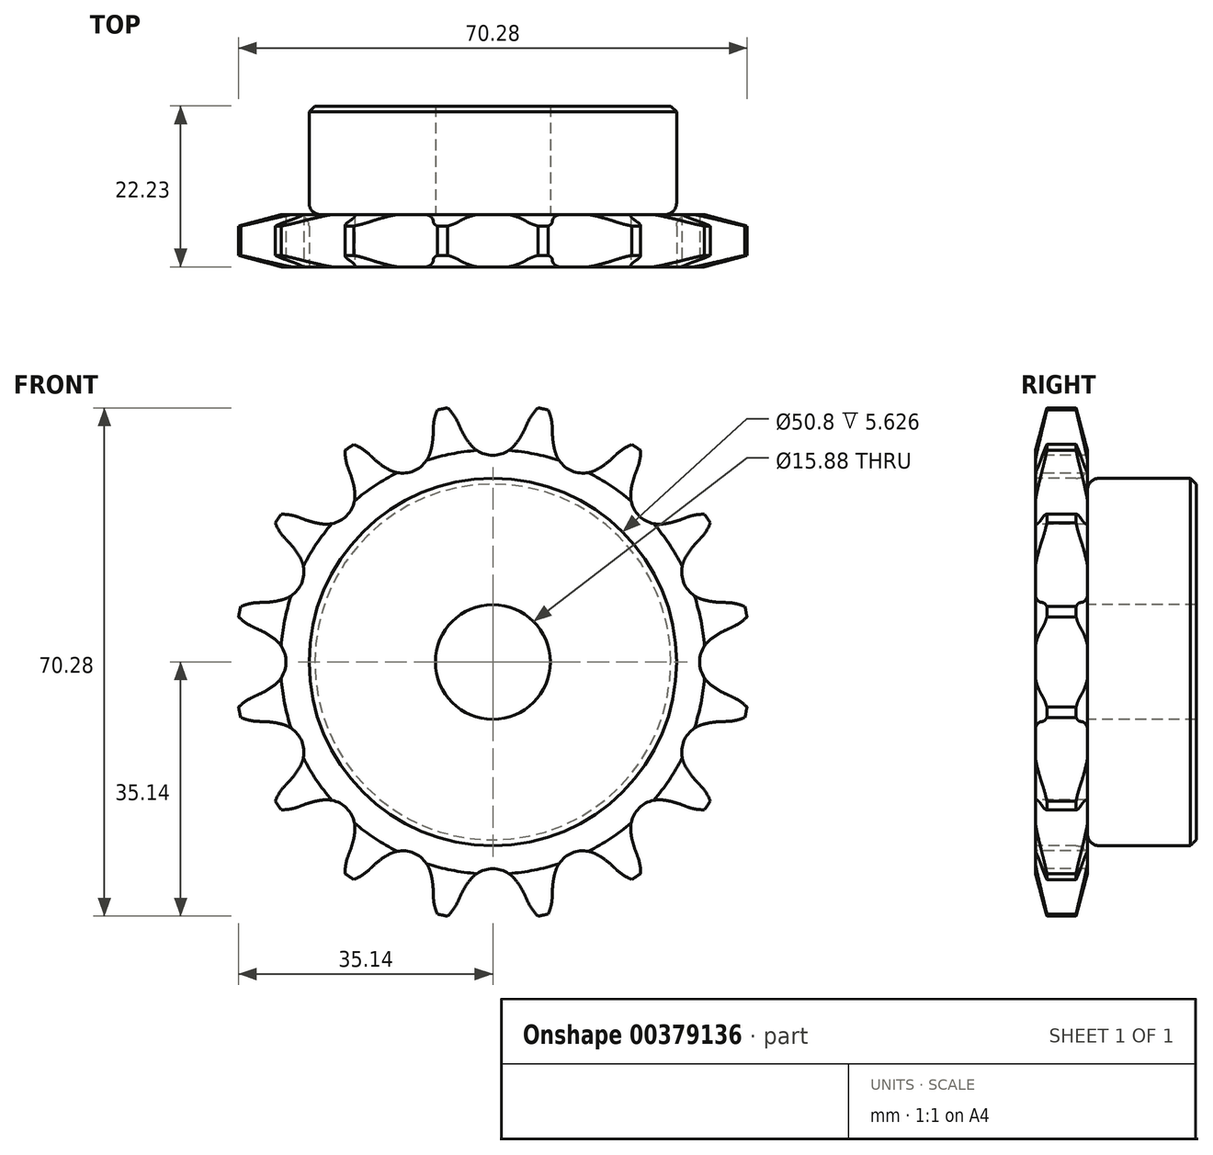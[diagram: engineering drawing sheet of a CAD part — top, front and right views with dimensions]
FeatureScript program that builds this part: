
annotation { "Feature Type Name" : "Feature", "Feature Type Description" : "" }
export const myFeature = defineFeature(function(context is Context, id is Id, definition is map)
    precondition{}
    {
        {
            var Q0;
            Q0=qCreatedBy(makeId("Right.planeOp"),FACE);
            var sketch = newSketch(context, id + "F0", { "sketchPlane" : qUnion([Q0])});
            skLineSegment(sketch, "E0", {"start": v(0, 0) * mm, "end": v(37.55, 0) * mm, "construction": true});
            skLineSegment(sketch, "E1.bottom", {"start": v(0, 7.94) * mm, "end": v(7.21, 7.94) * mm});
            skLineSegment(sketch, "E1.top", {"start": v(0, 35.69) * mm, "end": v(7.21, 35.69) * mm});
            skLineSegment(sketch, "E1.left", {"start": v(0, 7.94) * mm, "end": v(0, 35.69) * mm});
            skLineSegment(sketch, "E1.right", {"start": v(7.21, 7.94) * mm, "end": v(7.21, 35.69) * mm});
            skLineSegment(sketch, "E2.bottom", {"start": v(0, 7.94) * mm, "end": v(22.23, 7.94) * mm});
            skLineSegment(sketch, "E2.top", {"start": v(0, 25.4) * mm, "end": v(22.22, 25.4) * mm});
            skLineSegment(sketch, "E2.left", {"start": v(0, 7.94) * mm, "end": v(0, 25.4) * mm});
            skLineSegment(sketch, "E2.right", {"start": v(22.23, 7.94) * mm, "end": v(22.22, 25.4) * mm});
            skLineSegment(sketch, "E3.MirrorCS", {"start": v(0, -7.94) * mm, "end": v(7.21, -7.94) * mm});
            skLineSegment(sketch, "E4.MirrorCS", {"start": v(22.23, -7.94) * mm, "end": v(22.23, -25.4) * mm});
            skLineSegment(sketch, "E5.MirrorCS", {"start": v(0, -7.94) * mm, "end": v(0, -25.4) * mm});
            skLineSegment(sketch, "E6.MirrorCS", {"start": v(0, -25.4) * mm, "end": v(22.22, -25.4) * mm});
            skLineSegment(sketch, "E7.MirrorCS", {"start": v(0, -7.94) * mm, "end": v(22.23, -7.94) * mm});
            skLineSegment(sketch, "E8.MirrorCS", {"start": v(7.21, -7.94) * mm, "end": v(7.21, -35.69) * mm});
            skLineSegment(sketch, "E9.MirrorCS", {"start": v(0, -7.94) * mm, "end": v(0, -35.69) * mm});
            skLineSegment(sketch, "E10.MirrorCS", {"start": v(0, -35.69) * mm, "end": v(7.21, -35.69) * mm});
            skSolve(sketch);
        }
        {
            var Q0;
            {var subQ5=sQuery(id+"F0.wireOp",EDGE,"E2.right");Q0=makeQuery(id+"F0.imprint","IMPRINT",FACE,{"disambiguationData":[TD([[makeQuery(id+"F0.imprint","IMPRINT",EDGE,{"derivedFrom":subQ5}),1.0]])]});}
            var Q1;
            {var subQ5=sQuery(id+"F0.wireOp",EDGE,"E2.left");Q1=makeQuery(id+"F0.imprint","IMPRINT",FACE,{"disambiguationData":[TD([[makeQuery(id+"F0.imprint","IMPRINT",EDGE,{"derivedFrom":subQ5}),-1.0]])]});}
            var Q2;
            {var subQ0=sQuery(id+"F0.wireOp",EDGE,"E1.top");Q2=makeQuery(id+"F0.imprint","IMPRINT",FACE,{"disambiguationData":[TD([[makeQuery(id+"F0.imprint","IMPRINT",EDGE,{"derivedFrom":subQ0}),-1.0]])]});}
            var Q3;
            Q3=sQuery(id+"F0.wireOp",EDGE,"E0");
            revolve(context, id + "F1", {"entities" : qUnion([Q0, Q1, Q2]), "axis" : qUnion([Q3]), "revolveType" : RevolveType.FULL});
        }
        {
            var Q0;
            Q0=makeQuery(id+"F1.opRevolve","SWEPT_EDGE",EDGE,{"disambiguationData":[OSD([sQuery(id+"F0.wireOp",EDGE,"E1.right"),sQuery(id+"F0.wireOp",EDGE,"E2.top")])]});
            fillet(context, id + "F2", {"entities" : qUnion([Q0]), "radius" : 1.59 * mm, "tangentPropagation" : true, "allowEdgeOverflow" : false});
        }
        {
            var Q0;
            Q0=makeQuery(id+"F1.opRevolve","SWEPT_EDGE",EDGE,{"disambiguationData":[OSD([sQuery(id+"F0.wireOp",EDGE,"E2.top"),sQuery(id+"F0.wireOp",EDGE,"E2.right")])]});
            chamfer(context, id + "F3", {"entities" : qUnion([Q0]), "width" : 0.8 * mm, "tangentPropagation" : true});
        }
        {
            var Q0;
            Q0=makeQuery(id+"F1.opRevolve","SWEPT_EDGE",EDGE,{"disambiguationData":[OSD([sQuery(id+"F0.wireOp",EDGE,"E1.top"),sQuery(id+"F0.wireOp",EDGE,"E1.left")])]});
            var Q1;
            Q1=makeQuery(id+"F1.opRevolve","SWEPT_EDGE",EDGE,{"disambiguationData":[OSD([sQuery(id+"F0.wireOp",EDGE,"E1.top"),sQuery(id+"F0.wireOp",EDGE,"E1.right")])]});
            chamfer(context, id + "F4", {"entities" : qUnion([Q0, Q1]), "chamferType" : ChamferType.TWO_OFFSETS, "width1" : 6.35 * mm, "oppositeDirection" : false, "width2" : 1.59 * mm, "tangentPropagation" : true});
        }
        {
            var Q0;
            Q0=makeQuery(id+"F1.opRevolve","SWEPT_FACE",FACE,{"disambiguationData":[OSD([sQuery(id+"F0.wireOp",EDGE,"E1.left"),sQuery(id+"F0.wireOp",EDGE,"E2.left")])]});
            var sketch = newSketch(context, id + "F5", { "sketchPlane" : qUnion([Q0])});
            skCircle(sketch, "E11", {"center": v(0, 0) * mm, "radius": 32.55 * mm, "construction": true});
            skLineSegment(sketch, "E12", {"start": v(0, 0) * mm, "end": v(0, 32.55) * mm, "construction": true});
            skLineSegment(sketch, "E13", {"start": v(0, 32.55) * mm, "end": v(30.15, 32.55) * mm, "construction": true});
            skLineSegment(sketch, "E14", {"start": v(0, 32.55) * mm, "end": v(5, 36.56) * mm, "construction": true});
            skLineSegment(sketch, "E15", {"start": v(5, 36.56) * mm, "end": v(-4.46, 32.3) * mm, "construction": true});
            skLineSegment(sketch, "E16", {"start": v(-4.46, 32.3) * mm, "end": v(-4.82, 33.1) * mm});
            skLineSegment(sketch, "E17", {"start": v(0, 0) * mm, "end": v(-7.32, 35.97) * mm, "construction": true});
            skArc(sketch, "E18", {"start": v(-7.32, 35.97) * mm, "mid": v(-15.8, 26.06) * mm, "end": v(-4.82, 33.1) * mm, "construction": true});
            skArc(sketch, "E19", {"start": v(-4.82, 33.1) * mm, "mid": v(-5.86, 34.72) * mm, "end": v(-7.32, 35.97) * mm});
            skLineSegment(sketch, "E20", {"start": v(-4.82, 33.1) * mm, "end": v(-4.82, 33.1) * mm});
            skArc(sketch, "E21", {"start": v(-4.46, 32.3) * mm, "mid": v(-3.84, 31.14) * mm, "end": v(-3.1, 30.07) * mm});
            skArc(sketch, "E22", {"start": v(-3.1, 30.07) * mm, "mid": v(-0.38, 27.7) * mm, "end": v(2.99, 26.39) * mm});
            skLineSegment(sketch, "E23", {"start": v(-4.46, 32.3) * mm, "end": v(-4.46, 32.3) * mm});
            skArc(sketch, "E24", {"start": v(2.99, 26.39) * mm, "mid": v(11.44, 44.67) * mm, "end": v(-4.46, 32.3) * mm, "construction": true});
            skArc(sketch, "E25.MirrorCS", {"start": v(4.82, 33.1) * mm, "mid": v(5.86, 34.72) * mm, "end": v(7.32, 35.97) * mm});
            skArc(sketch, "E26.MirrorCS", {"start": v(4.46, 32.3) * mm, "mid": v(3.84, 31.14) * mm, "end": v(3.1, 30.07) * mm});
            skLineSegment(sketch, "E27.MirrorCS", {"start": v(4.46, 32.3) * mm, "end": v(4.82, 33.1) * mm});
            skArc(sketch, "E28", {"start": v(-3.1, 30.07) * mm, "mid": v(0, 28.59) * mm, "end": v(3.1, 30.07) * mm});
            skArc(sketch, "E29", {"start": v(3.1, 30.07) * mm, "mid": v(0, 36.51) * mm, "end": v(-3.1, 30.07) * mm, "construction": true});
            skArc(sketch, "E30.1.0", {"start": v(-16.48, 28.14) * mm, "mid": v(-15.47, 27.3) * mm, "end": v(-14.36, 26.6) * mm});
            skArc(sketch, "E30.1.1", {"start": v(-14.36, 26.6) * mm, "mid": v(-10.94, 26.41) * mm, "end": v(-8.65, 28.96) * mm});
            skArc(sketch, "E30.1.2", {"start": v(-8.24, 31.55) * mm, "mid": v(-8.37, 30.24) * mm, "end": v(-8.65, 28.96) * mm});
            skLineSegment(sketch, "E30.1.3", {"start": v(-8.24, 31.55) * mm, "end": v(-8.22, 32.42) * mm});
            skArc(sketch, "E30.1.4", {"start": v(-8.22, 32.42) * mm, "mid": v(-7.88, 34.32) * mm, "end": v(-7, 36.03) * mm});
            skLineSegment(sketch, "E30.1.5", {"start": v(-16.48, 28.14) * mm, "end": v(-17.12, 28.74) * mm});
            skArc(sketch, "E30.1.6", {"start": v(-17.12, 28.74) * mm, "mid": v(-18.7, 29.84) * mm, "end": v(-20.53, 30.43) * mm});
            skArc(sketch, "E30.2.0", {"start": v(-26, 19.69) * mm, "mid": v(-24.74, 19.3) * mm, "end": v(-23.45, 19.08) * mm});
            skArc(sketch, "E30.2.1", {"start": v(-23.45, 19.08) * mm, "mid": v(-20.21, 20.21) * mm, "end": v(-19.08, 23.45) * mm});
            skArc(sketch, "E30.2.2", {"start": v(-19.69, 26) * mm, "mid": v(-19.3, 24.74) * mm, "end": v(-19.08, 23.45) * mm});
            skLineSegment(sketch, "E30.2.3", {"start": v(-19.69, 26) * mm, "end": v(-20, 26.8) * mm});
            skArc(sketch, "E30.2.4", {"start": v(-20, 26.8) * mm, "mid": v(-20.41, 28.7) * mm, "end": v(-20.26, 30.61) * mm});
            skLineSegment(sketch, "E30.2.5", {"start": v(-26, 19.69) * mm, "end": v(-26.8, 20) * mm});
            skArc(sketch, "E30.2.6", {"start": v(-26.8, 20) * mm, "mid": v(-28.7, 20.41) * mm, "end": v(-30.61, 20.26) * mm});
            skArc(sketch, "E30.3.0", {"start": v(-31.55, 8.24) * mm, "mid": v(-30.24, 8.37) * mm, "end": v(-28.96, 8.65) * mm});
            skArc(sketch, "E30.3.1", {"start": v(-28.96, 8.65) * mm, "mid": v(-26.41, 10.94) * mm, "end": v(-26.6, 14.36) * mm});
            skArc(sketch, "E30.3.2", {"start": v(-28.14, 16.48) * mm, "mid": v(-27.3, 15.47) * mm, "end": v(-26.6, 14.36) * mm});
            skLineSegment(sketch, "E30.3.3", {"start": v(-28.14, 16.48) * mm, "end": v(-28.74, 17.12) * mm});
            skArc(sketch, "E30.3.4", {"start": v(-28.74, 17.12) * mm, "mid": v(-29.84, 18.7) * mm, "end": v(-30.43, 20.53) * mm});
            skLineSegment(sketch, "E30.3.5", {"start": v(-31.55, 8.24) * mm, "end": v(-32.42, 8.22) * mm});
            skArc(sketch, "E30.3.6", {"start": v(-32.42, 8.22) * mm, "mid": v(-34.32, 7.88) * mm, "end": v(-36.03, 7) * mm});
            skArc(sketch, "E30.4.0", {"start": v(-32.3, -4.46) * mm, "mid": v(-31.14, -3.84) * mm, "end": v(-30.07, -3.1) * mm});
            skArc(sketch, "E30.4.1", {"start": v(-30.07, -3.1) * mm, "mid": v(-28.59, 0) * mm, "end": v(-30.07, 3.1) * mm});
            skArc(sketch, "E30.4.2", {"start": v(-32.3, 4.46) * mm, "mid": v(-31.14, 3.84) * mm, "end": v(-30.07, 3.1) * mm});
            skLineSegment(sketch, "E30.4.3", {"start": v(-32.3, 4.46) * mm, "end": v(-33.1, 4.82) * mm});
            skArc(sketch, "E30.4.4", {"start": v(-33.1, 4.82) * mm, "mid": v(-34.72, 5.86) * mm, "end": v(-35.97, 7.32) * mm});
            skLineSegment(sketch, "E30.4.5", {"start": v(-32.3, -4.46) * mm, "end": v(-33.1, -4.82) * mm});
            skArc(sketch, "E30.4.6", {"start": v(-33.1, -4.82) * mm, "mid": v(-34.72, -5.86) * mm, "end": v(-35.97, -7.32) * mm});
            skArc(sketch, "E30.5.0", {"start": v(-28.14, -16.48) * mm, "mid": v(-27.3, -15.47) * mm, "end": v(-26.6, -14.36) * mm});
            skArc(sketch, "E30.5.1", {"start": v(-26.6, -14.36) * mm, "mid": v(-26.41, -10.94) * mm, "end": v(-28.96, -8.65) * mm});
            skArc(sketch, "E30.5.2", {"start": v(-31.55, -8.24) * mm, "mid": v(-30.24, -8.37) * mm, "end": v(-28.96, -8.65) * mm});
            skLineSegment(sketch, "E30.5.3", {"start": v(-31.55, -8.24) * mm, "end": v(-32.42, -8.22) * mm});
            skArc(sketch, "E30.5.4", {"start": v(-32.42, -8.22) * mm, "mid": v(-34.32, -7.88) * mm, "end": v(-36.03, -7) * mm});
            skLineSegment(sketch, "E30.5.5", {"start": v(-28.14, -16.48) * mm, "end": v(-28.74, -17.12) * mm});
            skArc(sketch, "E30.5.6", {"start": v(-28.74, -17.12) * mm, "mid": v(-29.84, -18.7) * mm, "end": v(-30.43, -20.53) * mm});
            skArc(sketch, "E30.6.0", {"start": v(-19.69, -26) * mm, "mid": v(-19.3, -24.74) * mm, "end": v(-19.08, -23.45) * mm});
            skArc(sketch, "E30.6.1", {"start": v(-19.08, -23.45) * mm, "mid": v(-20.21, -20.21) * mm, "end": v(-23.45, -19.08) * mm});
            skArc(sketch, "E30.6.2", {"start": v(-26, -19.69) * mm, "mid": v(-24.74, -19.3) * mm, "end": v(-23.45, -19.08) * mm});
            skLineSegment(sketch, "E30.6.3", {"start": v(-26, -19.69) * mm, "end": v(-26.8, -20) * mm});
            skArc(sketch, "E30.6.4", {"start": v(-26.8, -20) * mm, "mid": v(-28.7, -20.41) * mm, "end": v(-30.61, -20.26) * mm});
            skLineSegment(sketch, "E30.6.5", {"start": v(-19.69, -26) * mm, "end": v(-20, -26.8) * mm});
            skArc(sketch, "E30.6.6", {"start": v(-20, -26.8) * mm, "mid": v(-20.41, -28.7) * mm, "end": v(-20.26, -30.61) * mm});
            skArc(sketch, "E30.7.0", {"start": v(-8.24, -31.55) * mm, "mid": v(-8.37, -30.24) * mm, "end": v(-8.65, -28.96) * mm});
            skArc(sketch, "E30.7.1", {"start": v(-8.65, -28.96) * mm, "mid": v(-10.94, -26.41) * mm, "end": v(-14.36, -26.6) * mm});
            skArc(sketch, "E30.7.2", {"start": v(-16.48, -28.14) * mm, "mid": v(-15.47, -27.3) * mm, "end": v(-14.36, -26.6) * mm});
            skLineSegment(sketch, "E30.7.3", {"start": v(-16.48, -28.14) * mm, "end": v(-17.12, -28.74) * mm});
            skArc(sketch, "E30.7.4", {"start": v(-17.12, -28.74) * mm, "mid": v(-18.7, -29.84) * mm, "end": v(-20.53, -30.43) * mm});
            skLineSegment(sketch, "E30.7.5", {"start": v(-8.24, -31.55) * mm, "end": v(-8.22, -32.42) * mm});
            skArc(sketch, "E30.7.6", {"start": v(-8.22, -32.42) * mm, "mid": v(-7.88, -34.32) * mm, "end": v(-7, -36.03) * mm});
            skArc(sketch, "E30.8.0", {"start": v(4.46, -32.3) * mm, "mid": v(3.84, -31.14) * mm, "end": v(3.1, -30.07) * mm});
            skArc(sketch, "E30.8.1", {"start": v(3.1, -30.07) * mm, "mid": v(0, -28.59) * mm, "end": v(-3.1, -30.07) * mm});
            skArc(sketch, "E30.8.2", {"start": v(-4.46, -32.3) * mm, "mid": v(-3.84, -31.14) * mm, "end": v(-3.1, -30.07) * mm});
            skLineSegment(sketch, "E30.8.3", {"start": v(-4.46, -32.3) * mm, "end": v(-4.82, -33.1) * mm});
            skArc(sketch, "E30.8.4", {"start": v(-4.82, -33.1) * mm, "mid": v(-5.86, -34.72) * mm, "end": v(-7.32, -35.97) * mm});
            skLineSegment(sketch, "E30.8.5", {"start": v(4.46, -32.3) * mm, "end": v(4.82, -33.1) * mm});
            skArc(sketch, "E30.8.6", {"start": v(4.82, -33.1) * mm, "mid": v(5.86, -34.72) * mm, "end": v(7.32, -35.97) * mm});
            skArc(sketch, "E30.9.0", {"start": v(16.48, -28.14) * mm, "mid": v(15.47, -27.3) * mm, "end": v(14.36, -26.6) * mm});
            skArc(sketch, "E30.9.1", {"start": v(14.36, -26.6) * mm, "mid": v(10.94, -26.41) * mm, "end": v(8.65, -28.96) * mm});
            skArc(sketch, "E30.9.2", {"start": v(8.24, -31.55) * mm, "mid": v(8.37, -30.24) * mm, "end": v(8.65, -28.96) * mm});
            skLineSegment(sketch, "E30.9.3", {"start": v(8.24, -31.55) * mm, "end": v(8.22, -32.42) * mm});
            skArc(sketch, "E30.9.4", {"start": v(8.22, -32.42) * mm, "mid": v(7.88, -34.32) * mm, "end": v(7, -36.03) * mm});
            skLineSegment(sketch, "E30.9.5", {"start": v(16.48, -28.14) * mm, "end": v(17.12, -28.74) * mm});
            skArc(sketch, "E30.9.6", {"start": v(17.12, -28.74) * mm, "mid": v(18.7, -29.84) * mm, "end": v(20.53, -30.43) * mm});
            skArc(sketch, "E30.10.0", {"start": v(26, -19.69) * mm, "mid": v(24.74, -19.3) * mm, "end": v(23.45, -19.08) * mm});
            skArc(sketch, "E30.10.1", {"start": v(23.45, -19.08) * mm, "mid": v(20.21, -20.21) * mm, "end": v(19.08, -23.45) * mm});
            skArc(sketch, "E30.10.2", {"start": v(19.69, -26) * mm, "mid": v(19.3, -24.74) * mm, "end": v(19.08, -23.45) * mm});
            skLineSegment(sketch, "E30.10.3", {"start": v(19.69, -26) * mm, "end": v(20, -26.8) * mm});
            skArc(sketch, "E30.10.4", {"start": v(20, -26.8) * mm, "mid": v(20.41, -28.7) * mm, "end": v(20.26, -30.61) * mm});
            skLineSegment(sketch, "E30.10.5", {"start": v(26, -19.69) * mm, "end": v(26.8, -20) * mm});
            skArc(sketch, "E30.10.6", {"start": v(26.8, -20) * mm, "mid": v(28.7, -20.41) * mm, "end": v(30.61, -20.26) * mm});
            skArc(sketch, "E30.11.0", {"start": v(31.55, -8.24) * mm, "mid": v(30.24, -8.37) * mm, "end": v(28.96, -8.65) * mm});
            skArc(sketch, "E30.11.1", {"start": v(28.96, -8.65) * mm, "mid": v(26.41, -10.94) * mm, "end": v(26.6, -14.36) * mm});
            skArc(sketch, "E30.11.2", {"start": v(28.14, -16.48) * mm, "mid": v(27.3, -15.47) * mm, "end": v(26.6, -14.36) * mm});
            skLineSegment(sketch, "E30.11.3", {"start": v(28.14, -16.48) * mm, "end": v(28.74, -17.12) * mm});
            skArc(sketch, "E30.11.4", {"start": v(28.74, -17.12) * mm, "mid": v(29.84, -18.7) * mm, "end": v(30.43, -20.53) * mm});
            skLineSegment(sketch, "E30.11.5", {"start": v(31.55, -8.24) * mm, "end": v(32.42, -8.22) * mm});
            skArc(sketch, "E30.11.6", {"start": v(32.42, -8.22) * mm, "mid": v(34.32, -7.88) * mm, "end": v(36.03, -7) * mm});
            skArc(sketch, "E30.12.0", {"start": v(32.3, 4.46) * mm, "mid": v(31.14, 3.84) * mm, "end": v(30.07, 3.1) * mm});
            skArc(sketch, "E30.12.1", {"start": v(30.07, 3.1) * mm, "mid": v(28.59, 0) * mm, "end": v(30.07, -3.1) * mm});
            skArc(sketch, "E30.12.2", {"start": v(32.3, -4.46) * mm, "mid": v(31.14, -3.84) * mm, "end": v(30.07, -3.1) * mm});
            skLineSegment(sketch, "E30.12.3", {"start": v(32.3, -4.46) * mm, "end": v(33.1, -4.82) * mm});
            skArc(sketch, "E30.12.4", {"start": v(33.1, -4.82) * mm, "mid": v(34.72, -5.86) * mm, "end": v(35.97, -7.32) * mm});
            skLineSegment(sketch, "E30.12.5", {"start": v(32.3, 4.46) * mm, "end": v(33.1, 4.82) * mm});
            skArc(sketch, "E30.12.6", {"start": v(33.1, 4.82) * mm, "mid": v(34.72, 5.86) * mm, "end": v(35.97, 7.32) * mm});
            skArc(sketch, "E30.13.0", {"start": v(28.14, 16.48) * mm, "mid": v(27.3, 15.47) * mm, "end": v(26.6, 14.36) * mm});
            skArc(sketch, "E30.13.1", {"start": v(26.6, 14.36) * mm, "mid": v(26.41, 10.94) * mm, "end": v(28.96, 8.65) * mm});
            skArc(sketch, "E30.13.2", {"start": v(31.55, 8.24) * mm, "mid": v(30.24, 8.37) * mm, "end": v(28.96, 8.65) * mm});
            skLineSegment(sketch, "E30.13.3", {"start": v(31.55, 8.24) * mm, "end": v(32.42, 8.22) * mm});
            skArc(sketch, "E30.13.4", {"start": v(32.42, 8.22) * mm, "mid": v(34.32, 7.88) * mm, "end": v(36.03, 7) * mm});
            skLineSegment(sketch, "E30.13.5", {"start": v(28.14, 16.48) * mm, "end": v(28.74, 17.12) * mm});
            skArc(sketch, "E30.13.6", {"start": v(28.74, 17.12) * mm, "mid": v(29.84, 18.7) * mm, "end": v(30.43, 20.53) * mm});
            skArc(sketch, "E30.14.0", {"start": v(19.69, 26) * mm, "mid": v(19.3, 24.74) * mm, "end": v(19.08, 23.45) * mm});
            skArc(sketch, "E30.14.1", {"start": v(19.08, 23.45) * mm, "mid": v(20.21, 20.21) * mm, "end": v(23.45, 19.08) * mm});
            skArc(sketch, "E30.14.2", {"start": v(26, 19.69) * mm, "mid": v(24.74, 19.3) * mm, "end": v(23.45, 19.08) * mm});
            skLineSegment(sketch, "E30.14.3", {"start": v(26, 19.69) * mm, "end": v(26.8, 20) * mm});
            skArc(sketch, "E30.14.4", {"start": v(26.8, 20) * mm, "mid": v(28.7, 20.41) * mm, "end": v(30.61, 20.26) * mm});
            skLineSegment(sketch, "E30.14.5", {"start": v(19.69, 26) * mm, "end": v(20, 26.8) * mm});
            skArc(sketch, "E30.14.6", {"start": v(20, 26.8) * mm, "mid": v(20.41, 28.7) * mm, "end": v(20.26, 30.61) * mm});
            skArc(sketch, "E30.15.0", {"start": v(8.24, 31.55) * mm, "mid": v(8.37, 30.24) * mm, "end": v(8.65, 28.96) * mm});
            skArc(sketch, "E30.15.1", {"start": v(8.65, 28.96) * mm, "mid": v(10.94, 26.41) * mm, "end": v(14.36, 26.6) * mm});
            skArc(sketch, "E30.15.2", {"start": v(16.48, 28.14) * mm, "mid": v(15.47, 27.3) * mm, "end": v(14.36, 26.6) * mm});
            skLineSegment(sketch, "E30.15.3", {"start": v(16.48, 28.14) * mm, "end": v(17.12, 28.74) * mm});
            skArc(sketch, "E30.15.4", {"start": v(17.12, 28.74) * mm, "mid": v(18.7, 29.84) * mm, "end": v(20.53, 30.43) * mm});
            skLineSegment(sketch, "E30.15.5", {"start": v(8.24, 31.55) * mm, "end": v(8.22, 32.42) * mm});
            skArc(sketch, "E30.15.6", {"start": v(8.22, 32.42) * mm, "mid": v(7.88, 34.32) * mm, "end": v(7, 36.03) * mm});
            skSolve(sketch);
        }
        {
            var Q0;
            Q0 = qSketchRegion(id + "F5", true);
            extrude(context, id + "F6", {"entities" : qUnion([Q0]), "operationType" : NewBodyOperationType.INTERSECT, "endBound" : BoundingType.THROUGH_ALL, "oppositeDirection" : true, "depth" : 25.4 * mm});
        }
    });
